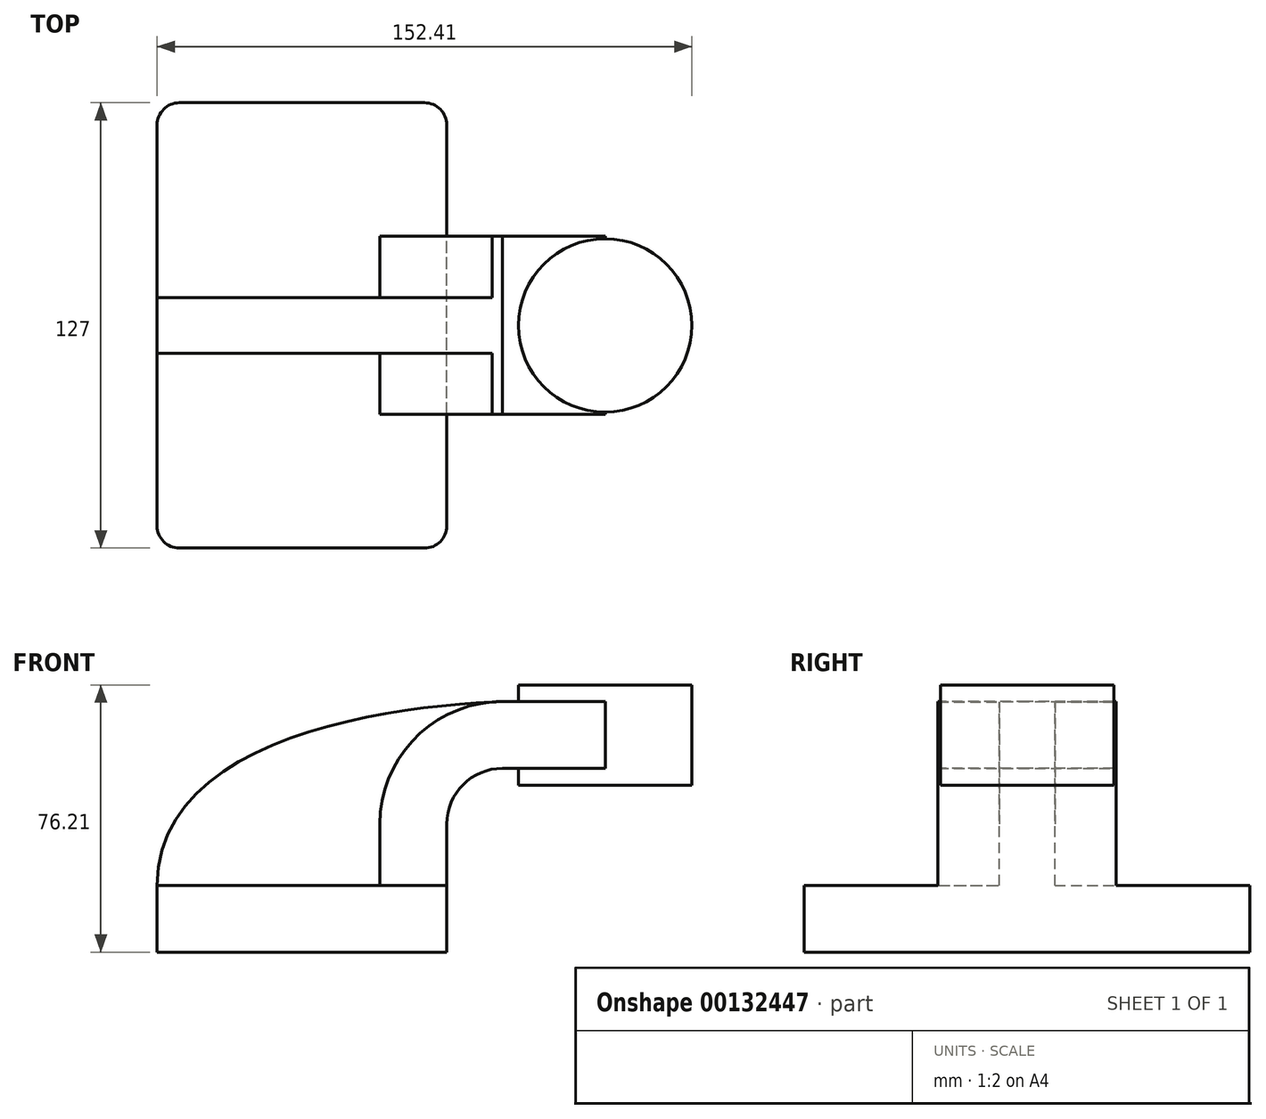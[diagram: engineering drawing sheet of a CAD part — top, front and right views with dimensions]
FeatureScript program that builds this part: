
annotation { "Feature Type Name" : "Feature", "Feature Type Description" : "" }
export const myFeature = defineFeature(function(context is Context, id is Id, definition is map)
    precondition{}
    {
        {
            var Q0;
            Q0=qCreatedBy(makeId("Front.planeOp"),FACE);
            var sketch = newSketch(context, id + "F0", { "sketchPlane" : qUnion([Q0])});
            skLineSegment(sketch, "E0.bottom", {"start": v(41.28, -9.52) * mm, "end": v(-41.27, -9.53) * mm});
            skLineSegment(sketch, "E0.top", {"start": v(41.27, 9.53) * mm, "end": v(-41.28, 9.53) * mm});
            skLineSegment(sketch, "E0.left", {"start": v(41.28, -9.52) * mm, "end": v(41.28, 9.53) * mm});
            skLineSegment(sketch, "E0.right", {"start": v(-41.27, -9.52) * mm, "end": v(-41.28, 9.53) * mm});
            skPoint(sketch, "E0.middle", {"position": v(0, 0) * mm});
            skLineSegment(sketch, "E1.bottom", {"start": v(111.12, 38.1) * mm, "end": v(60.32, 38.1) * mm});
            skLineSegment(sketch, "E1.top", {"start": v(111.13, 66.67) * mm, "end": v(60.33, 66.67) * mm});
            skLineSegment(sketch, "E1.left", {"start": v(111.13, 38.1) * mm, "end": v(111.13, 66.67) * mm});
            skLineSegment(sketch, "E1.right", {"start": v(60.32, 38.1) * mm, "end": v(60.33, 66.67) * mm});
            skPoint(sketch, "E1.middle", {"position": v(85.72, 52.39) * mm});
            skLineSegment(sketch, "E2", {"start": v(41.27, 9.53) * mm, "end": v(41.27, 27) * mm});
            skArc(sketch, "E3", {"start": v(41.27, 27) * mm, "mid": v(45.92, 38.23) * mm, "end": v(57.15, 42.88) * mm});
            skLineSegment(sketch, "E4", {"start": v(57.15, 42.88) * mm, "end": v(86.4, 42.88) * mm});
            skLineSegment(sketch, "E5.0", {"start": v(57.15, 61.93) * mm, "end": v(86.4, 61.93) * mm});
            skArc(sketch, "E5.1", {"start": v(22.22, 27) * mm, "mid": v(32.45, 51.7) * mm, "end": v(57.15, 61.93) * mm});
            skLineSegment(sketch, "E5.2", {"start": v(22.22, 9.53) * mm, "end": v(22.22, 27) * mm});
            skLineSegment(sketch, "E6", {"start": v(86.4, 38.1) * mm, "end": v(86.4, 66.67) * mm});
            skPoint(sketch, "E6.startSnap0", {"position": v(85.72, 38.1) * mm});
            skFitSpline(sketch, "E7", {"points": [v(-41.28, 9.53) * mm, v(57.15, 61.93) * mm], "startDerivative": vector(0.77, 127.36) * mm, "endDerivative": vector(96.74, 3.6) * mm});
            skSolve(sketch);
        }
        {
            var Q0;
            Q0=makeQuery(id+"F0.imprint","IMPRINT",FACE,{"disambiguationData":[TD([[makeQuery(id+"F0.imprint","IMPRINT",EDGE,{"derivedFrom":sQuery(id+"F0.wireOp",EDGE,"E0.bottom")}),-1.0]])]});
            extrude(context, id + "F1", {"entities" : qUnion([Q0]), "endBound" : BoundingType.SYMMETRIC, "depth" : 127 * mm});
        }
        {
            var Q0;
            {var subQ1=sQuery(id+"F0.wireOp",EDGE,"E2");Q0=makeQuery(id+"F0.imprint","IMPRINT",FACE,{"disambiguationData":[TD([[makeQuery(id+"F0.imprint","IMPRINT",EDGE,{"derivedFrom":subQ1}),1.0]])]});}
            var Q1;
            {var subQ0=sQuery(id+"F0.wireOp",EDGE,"E4");var subQ1=sQuery(id+"F0.wireOp",EDGE,"E1.right");var subQ2=makeQuery(id+"F0.imprint","INTERSECT",VERTEX,{"derivedFrom":[subQ1,subQ0]});Q1=makeQuery(id+"F0.imprint","IMPRINT",FACE,{"disambiguationData":[TD([[makeQuery(id+"F0.imprint","IMPRINT",EDGE,{"disambiguationData":[TD([[subQ2,-1.0]])],"derivedFrom":subQ1}),-1.0]])]});}
            extrude(context, id + "F2", {"entities" : qUnion([Q0, Q1]), "operationType" : NewBodyOperationType.ADD, "endBound" : BoundingType.SYMMETRIC, "depth" : 50.8 * mm});
        }
        {
            var Q0;
            {var subQ3=sQuery(id+"F0.wireOp",EDGE,"E5.2");Q0=makeQuery(id+"F0.imprint","IMPRINT",FACE,{"disambiguationData":[TD([[makeQuery(id+"F0.imprint","IMPRINT",EDGE,{"derivedFrom":subQ3}),1.0]])]});}
            extrude(context, id + "F3", {"entities" : qUnion([Q0]), "operationType" : NewBodyOperationType.ADD, "endBound" : BoundingType.SYMMETRIC, "depth" : 15.88 * mm});
        }
        {
            var Q0;
            {var subQ0=sQuery(id+"F0.wireOp",EDGE,"E1.left");Q0=makeQuery(id+"F0.imprint","IMPRINT",FACE,{"disambiguationData":[TD([[makeQuery(id+"F0.imprint","IMPRINT",EDGE,{"derivedFrom":subQ0}),1.0]])]});}
            var Q1;
            Q1=sQuery(id+"F0.wireOp",EDGE,"E6");
            revolve(context, id + "F4", {"operationType" : NewBodyOperationType.ADD, "entities" : qUnion([Q0]), "axis" : qUnion([Q1]), "revolveType" : RevolveType.FULL});
        }
        {
            var Q0;
            Q0=makeQuery(id+"F1.opExtrude","CAP_EDGE",EDGE,{"disambiguationData":[OSD([sQuery(id+"F0.wireOp",EDGE,"E0.left")])],"isStart":false});
            var Q1;
            Q1=makeQuery(id+"F1.opExtrude","CAP_EDGE",EDGE,{"disambiguationData":[OSD([sQuery(id+"F0.wireOp",EDGE,"E0.right")])],"isStart":false});
            var Q2;
            Q2=makeQuery(id+"F1.opExtrude","CAP_EDGE",EDGE,{"disambiguationData":[OSD([sQuery(id+"F0.wireOp",EDGE,"E0.left")])],"isStart":true});
            var Q3;
            Q3=makeQuery(id+"F1.opExtrude","CAP_EDGE",EDGE,{"disambiguationData":[OSD([sQuery(id+"F0.wireOp",EDGE,"E0.right")])],"isStart":true});
            fillet(context, id + "F5", {"entities" : qUnion([Q0, Q1, Q2, Q3]), "radius" : 6.35 * mm, "tangentPropagation" : true, "allowEdgeOverflow" : false});
        }
    });
